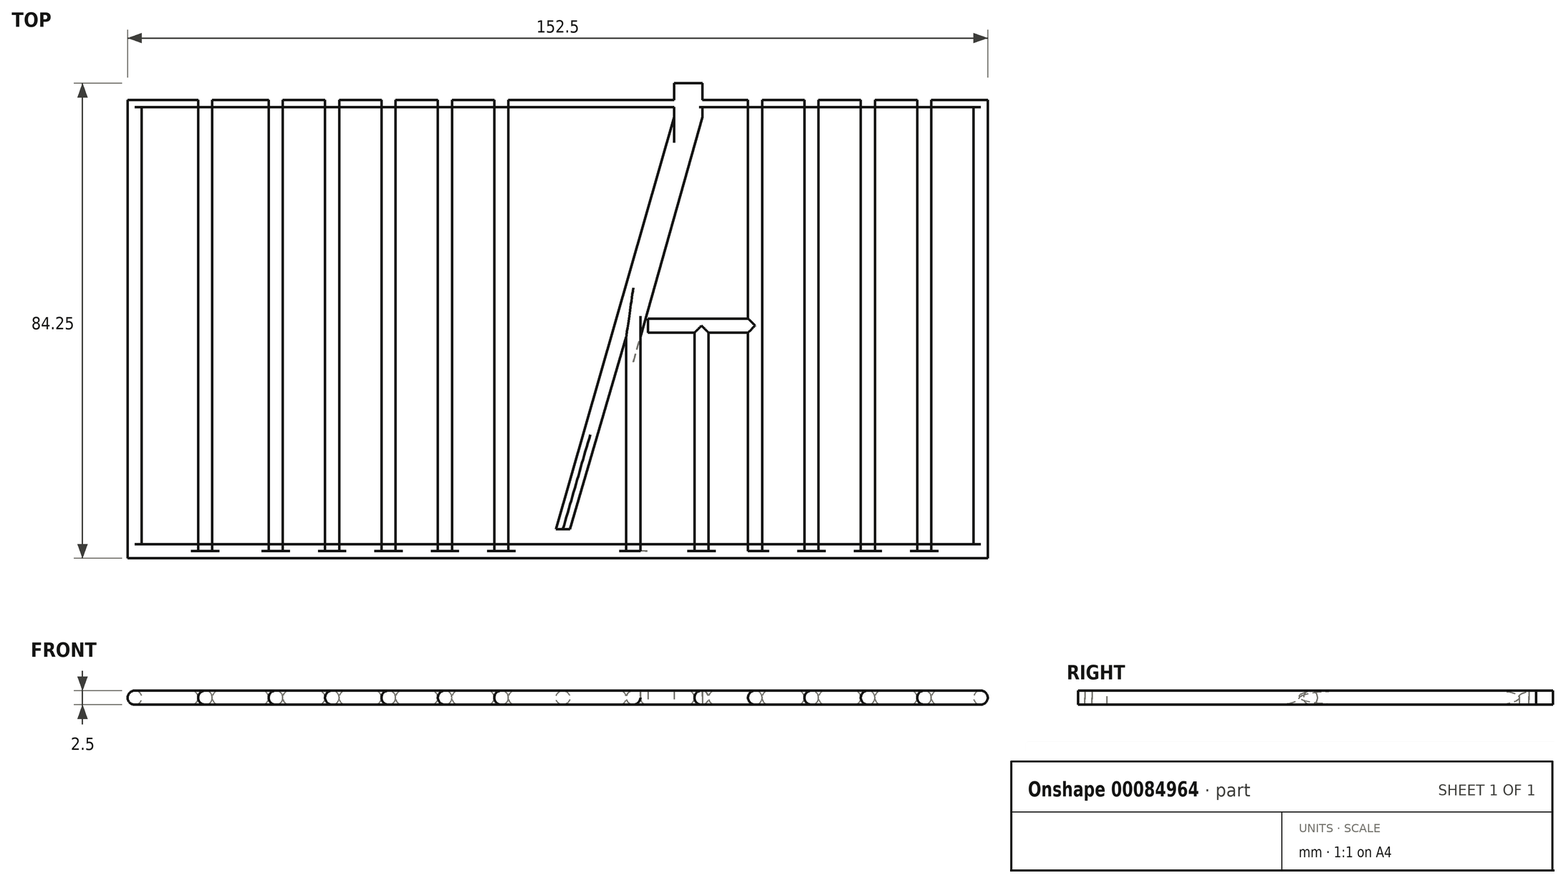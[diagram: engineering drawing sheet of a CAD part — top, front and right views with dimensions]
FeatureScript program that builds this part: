
annotation { "Feature Type Name" : "Feature", "Feature Type Description" : "" }
export const myFeature = defineFeature(function(context is Context, id is Id, definition is map)
    precondition{}
    {
        {
            var Q0;
            Q0=qCreatedBy(makeId("Top.planeOp"),FACE);
            var sketch = newSketch(context, id + "F0", { "sketchPlane" : qUnion([Q0])});
            skLineSegment(sketch, "E0", {"start": v(0, 0) * mm, "end": v(75, 0) * mm});
            skLineSegment(sketch, "E1", {"start": v(0, 0) * mm, "end": v(-75, 0) * mm});
            skLineSegment(sketch, "E2", {"start": v(-75, 0) * mm, "end": v(-75, 80) * mm});
            skLineSegment(sketch, "E3", {"start": v(-75, 80) * mm, "end": v(75, 80) * mm});
            skLineSegment(sketch, "E4", {"start": v(75, 80) * mm, "end": v(75, 0) * mm});
            skLineSegment(sketch, "E5.bottom", {"start": v(-73.75, 0) * mm, "end": v(-76.25, 0) * mm});
            skLineSegment(sketch, "E5.top", {"start": v(-73.75, 80) * mm, "end": v(-76.25, 80) * mm});
            skLineSegment(sketch, "E5.left", {"start": v(-73.75, 0) * mm, "end": v(-73.75, 80) * mm});
            skLineSegment(sketch, "E5.right", {"start": v(-76.25, 0) * mm, "end": v(-76.25, 80) * mm});
            skPoint(sketch, "E5.middle", {"position": v(-75, 40) * mm});
            skLineSegment(sketch, "E6.bottom", {"start": v(76.25, 0) * mm, "end": v(73.75, 0) * mm});
            skLineSegment(sketch, "E6.top", {"start": v(76.25, 80) * mm, "end": v(73.75, 80) * mm});
            skLineSegment(sketch, "E6.left", {"start": v(76.25, 0) * mm, "end": v(76.25, 80) * mm});
            skLineSegment(sketch, "E6.right", {"start": v(73.75, 0) * mm, "end": v(73.75, 80) * mm});
            skPoint(sketch, "E6.middle", {"position": v(75, 40) * mm});
            skLineSegment(sketch, "E7.bottom", {"start": v(-76.25, 81.25) * mm, "end": v(76.25, 81.25) * mm});
            skLineSegment(sketch, "E7.top", {"start": v(-76.25, 78.75) * mm, "end": v(76.25, 78.75) * mm});
            skLineSegment(sketch, "E7.left", {"start": v(-76.25, 81.25) * mm, "end": v(-76.25, 78.75) * mm});
            skLineSegment(sketch, "E7.right", {"start": v(76.25, 81.25) * mm, "end": v(76.25, 78.75) * mm});
            skPoint(sketch, "E7.middle", {"position": v(0, 80) * mm});
            skLineSegment(sketch, "E8.bottom", {"start": v(-76.25, -1.25) * mm, "end": v(76.25, -1.25) * mm});
            skLineSegment(sketch, "E8.top", {"start": v(-76.25, 1.25) * mm, "end": v(76.25, 1.25) * mm});
            skLineSegment(sketch, "E8.left", {"start": v(-76.25, -1.25) * mm, "end": v(-76.25, 1.25) * mm});
            skLineSegment(sketch, "E8.right", {"start": v(76.25, -1.25) * mm, "end": v(76.25, 1.25) * mm});
            skPoint(sketch, "E8.middle", {"position": v(0, 0) * mm});
            skLineSegment(sketch, "E9.bottom", {"start": v(-61.25, 0) * mm, "end": v(-63.75, 0) * mm});
            skLineSegment(sketch, "E9.top", {"start": v(-61.25, 80) * mm, "end": v(-63.75, 80) * mm});
            skLineSegment(sketch, "E9.left", {"start": v(-61.25, 0) * mm, "end": v(-61.25, 80) * mm});
            skLineSegment(sketch, "E9.right", {"start": v(-63.75, 0) * mm, "end": v(-63.75, 80) * mm});
            skPoint(sketch, "E9.middle", {"position": v(-62.5, 40) * mm});
            skLineSegment(sketch, "E10.bottom", {"start": v(-48.75, 0) * mm, "end": v(-51.25, 0) * mm});
            skLineSegment(sketch, "E10.top", {"start": v(-48.75, 80) * mm, "end": v(-51.25, 80) * mm});
            skLineSegment(sketch, "E10.left", {"start": v(-48.75, 0) * mm, "end": v(-48.75, 80) * mm});
            skLineSegment(sketch, "E10.right", {"start": v(-51.25, 0) * mm, "end": v(-51.25, 80) * mm});
            skPoint(sketch, "E10.middle", {"position": v(-50, 40) * mm});
            skLineSegment(sketch, "E11.bottom", {"start": v(14.66, 0) * mm, "end": v(12.16, 0) * mm});
            skLineSegment(sketch, "E11.top", {"start": v(14.66, 38) * mm, "end": v(12.16, 38) * mm});
            skLineSegment(sketch, "E11.left", {"start": v(14.66, 0) * mm, "end": v(14.66, 38) * mm});
            skLineSegment(sketch, "E11.right", {"start": v(12.16, 0) * mm, "end": v(12.16, 38) * mm});
            skPoint(sketch, "E11.middle", {"position": v(13.4, 19) * mm});
            skLineSegment(sketch, "E12.bottom", {"start": v(25.63, 77) * mm, "end": v(20.63, 77) * mm});
            skLineSegment(sketch, "E12.top", {"start": v(25.63, 83) * mm, "end": v(20.63, 83) * mm});
            skLineSegment(sketch, "E12.left", {"start": v(25.63, 77) * mm, "end": v(25.63, 83) * mm});
            skLineSegment(sketch, "E12.right", {"start": v(20.63, 77) * mm, "end": v(20.63, 83) * mm});
            skPoint(sketch, "E12.middle", {"position": v(23.13, 80) * mm});
            skLineSegment(sketch, "E13", {"start": v(25.63, 77) * mm, "end": v(14.66, 38) * mm});
            skLineSegment(sketch, "E14", {"start": v(12.16, 38) * mm, "end": v(23.13, 77) * mm});
            skLineSegment(sketch, "E15", {"start": v(12.16, 38) * mm, "end": v(2.16, 3.89) * mm});
            skLineSegment(sketch, "E16", {"start": v(20.63, 77) * mm, "end": v(-0.34, 3.89) * mm});
            skLineSegment(sketch, "E17", {"start": v(-0.34, 3.89) * mm, "end": v(2.16, 3.89) * mm});
            skLineSegment(sketch, "E18.bottom", {"start": v(-38.75, 0) * mm, "end": v(-41.25, 0) * mm});
            skLineSegment(sketch, "E18.top", {"start": v(-38.75, 80) * mm, "end": v(-41.25, 80) * mm});
            skLineSegment(sketch, "E18.left", {"start": v(-38.75, 0) * mm, "end": v(-38.75, 80) * mm});
            skLineSegment(sketch, "E18.right", {"start": v(-41.25, 0) * mm, "end": v(-41.25, 80) * mm});
            skPoint(sketch, "E18.middle", {"position": v(-40, 40) * mm});
            skLineSegment(sketch, "E19.bottom", {"start": v(-28.75, 0) * mm, "end": v(-31.25, 0) * mm});
            skLineSegment(sketch, "E19.top", {"start": v(-28.75, 80) * mm, "end": v(-31.25, 80) * mm});
            skLineSegment(sketch, "E19.left", {"start": v(-28.75, 0) * mm, "end": v(-28.75, 80) * mm});
            skLineSegment(sketch, "E19.right", {"start": v(-31.25, 0) * mm, "end": v(-31.25, 80) * mm});
            skPoint(sketch, "E19.middle", {"position": v(-30, 40) * mm});
            skLineSegment(sketch, "E20.bottom", {"start": v(-18.75, 0) * mm, "end": v(-21.25, 0) * mm});
            skLineSegment(sketch, "E20.top", {"start": v(-18.75, 80) * mm, "end": v(-21.25, 80) * mm});
            skLineSegment(sketch, "E20.left", {"start": v(-18.75, 0) * mm, "end": v(-18.75, 80) * mm});
            skLineSegment(sketch, "E20.right", {"start": v(-21.25, 0) * mm, "end": v(-21.25, 80) * mm});
            skPoint(sketch, "E20.middle", {"position": v(-20, 40) * mm});
            skLineSegment(sketch, "E21.bottom", {"start": v(-8.75, 0) * mm, "end": v(-11.25, 0) * mm});
            skLineSegment(sketch, "E21.top", {"start": v(-8.75, 80) * mm, "end": v(-11.25, 80) * mm});
            skLineSegment(sketch, "E21.left", {"start": v(-8.75, 0) * mm, "end": v(-8.75, 80) * mm});
            skLineSegment(sketch, "E21.right", {"start": v(-11.25, 0) * mm, "end": v(-11.25, 80) * mm});
            skPoint(sketch, "E21.middle", {"position": v(-10, 40) * mm});
            skLineSegment(sketch, "E22.bottom", {"start": v(66.25, 0) * mm, "end": v(63.75, 0) * mm});
            skLineSegment(sketch, "E22.top", {"start": v(66.25, 80) * mm, "end": v(63.75, 80) * mm});
            skLineSegment(sketch, "E22.left", {"start": v(66.25, 0) * mm, "end": v(66.25, 80) * mm});
            skLineSegment(sketch, "E22.right", {"start": v(63.75, 0) * mm, "end": v(63.75, 80) * mm});
            skPoint(sketch, "E22.middle", {"position": v(65, 40) * mm});
            skLineSegment(sketch, "E23.bottom", {"start": v(56.25, 0) * mm, "end": v(53.75, 0) * mm});
            skLineSegment(sketch, "E23.top", {"start": v(56.25, 80) * mm, "end": v(53.75, 80) * mm});
            skLineSegment(sketch, "E23.left", {"start": v(56.25, 0) * mm, "end": v(56.25, 80) * mm});
            skLineSegment(sketch, "E23.right", {"start": v(53.75, 0) * mm, "end": v(53.75, 80) * mm});
            skPoint(sketch, "E23.middle", {"position": v(55, 40) * mm});
            skLineSegment(sketch, "E24.bottom", {"start": v(46.25, 0) * mm, "end": v(43.75, 0) * mm});
            skLineSegment(sketch, "E24.top", {"start": v(46.25, 80) * mm, "end": v(43.75, 80) * mm});
            skLineSegment(sketch, "E24.left", {"start": v(46.25, 0) * mm, "end": v(46.25, 80) * mm});
            skLineSegment(sketch, "E24.right", {"start": v(43.75, 0) * mm, "end": v(43.75, 80) * mm});
            skPoint(sketch, "E24.middle", {"position": v(45, 40) * mm});
            skLineSegment(sketch, "E25.bottom", {"start": v(36.25, 0) * mm, "end": v(33.75, 0) * mm});
            skLineSegment(sketch, "E25.top", {"start": v(36.25, 80) * mm, "end": v(33.75, 80) * mm});
            skLineSegment(sketch, "E25.left", {"start": v(36.25, 0) * mm, "end": v(36.25, 80) * mm});
            skLineSegment(sketch, "E25.right", {"start": v(33.75, 0) * mm, "end": v(33.75, 80) * mm});
            skPoint(sketch, "E25.middle", {"position": v(35, 40) * mm});
            skPoint(sketch, "E25.middle.positionSnap0", {"position": v(43.75, 40) * mm});
            skPoint(sketch, "E25.centerSnap0", {"position": v(43.75, 40) * mm});
            skLineSegment(sketch, "E26.bottom", {"start": v(35, 38.75) * mm, "end": v(16, 38.75) * mm});
            skLineSegment(sketch, "E26.top", {"start": v(35, 41.25) * mm, "end": v(16, 41.25) * mm});
            skLineSegment(sketch, "E26.left", {"start": v(35, 38.75) * mm, "end": v(35, 41.25) * mm});
            skLineSegment(sketch, "E26.right", {"start": v(16, 38.75) * mm, "end": v(16, 41.25) * mm});
            skPoint(sketch, "E26.middle", {"position": v(25.5, 40) * mm});
            skLineSegment(sketch, "E27.bottom", {"start": v(26.75, 0) * mm, "end": v(24.25, 0) * mm});
            skLineSegment(sketch, "E27.top", {"start": v(26.75, 40) * mm, "end": v(24.25, 40) * mm});
            skLineSegment(sketch, "E27.left", {"start": v(26.75, 0) * mm, "end": v(26.75, 40) * mm});
            skLineSegment(sketch, "E27.right", {"start": v(24.25, 0) * mm, "end": v(24.25, 40) * mm});
            skPoint(sketch, "E27.middle", {"position": v(25.5, 20) * mm});
            skSolve(sketch);
        }
        {
            var Q0;
            {var subQ0=sQuery(id+"F0.wireOp",EDGE,"E8.bottom");Q0=makeQuery(id+"F0.imprint","IMPRINT",FACE,{"disambiguationData":[TD([[makeQuery(id+"F0.imprint","IMPRINT",EDGE,{"derivedFrom":subQ0}),1.0]])]});}
            var Q1;
            {var subQ3=sQuery(id+"F0.wireOp",EDGE,"E8.top");var subQ7=sQuery(id+"F0.wireOp",EDGE,"E21.left");var subQ9=makeQuery(id+"F0.imprint","INTERSECT",VERTEX,{"derivedFrom":[subQ3,subQ7]});Q1=makeQuery(id+"F0.imprint","IMPRINT",FACE,{"disambiguationData":[TD([[makeQuery(id+"F0.imprint","IMPRINT",EDGE,{"disambiguationData":[TD([[subQ9,-1.0]])],"derivedFrom":subQ3}),-1.0]])]});}
            var Q2;
            {var subQ5=sQuery(id+"F0.wireOp",EDGE,"E11.bottom");Q2=makeQuery(id+"F0.imprint","IMPRINT",FACE,{"disambiguationData":[TD([[makeQuery(id+"F0.imprint","IMPRINT",EDGE,{"derivedFrom":subQ5}),-1.0]])]});}
            var Q3;
            {var subQ0=sQuery(id+"F0.wireOp",EDGE,"E11.left");var subQ5=sQuery(id+"F0.wireOp",EDGE,"E8.top");var subQ6=makeQuery(id+"F0.imprint","INTERSECT",VERTEX,{"derivedFrom":[subQ5,subQ0]});Q3=makeQuery(id+"F0.imprint","IMPRINT",FACE,{"disambiguationData":[TD([[makeQuery(id+"F0.imprint","IMPRINT",EDGE,{"disambiguationData":[TD([[subQ6,-1.0]])],"derivedFrom":subQ5}),-1.0]])]});}
            var Q4;
            {var subQ5=sQuery(id+"F0.wireOp",EDGE,"E11.top");Q4=makeQuery(id+"F0.imprint","IMPRINT",FACE,{"disambiguationData":[TD([[makeQuery(id+"F0.imprint","IMPRINT",EDGE,{"derivedFrom":subQ5}),1.0]])]});}
            var Q5;
            {var subQ1=sQuery(id+"F0.wireOp",EDGE,"E14");Q5=makeQuery(id+"F0.imprint","IMPRINT",FACE,{"disambiguationData":[TD([[makeQuery(id+"F0.imprint","IMPRINT",EDGE,{"derivedFrom":subQ1}),1.0]])]});}
            var Q6;
            Q6=makeQuery(id+"F0.imprint","IMPRINT",FACE,{"disambiguationData":[TD([[makeQuery(id+"F0.imprint","IMPRINT",EDGE,{"derivedFrom":sQuery(id+"F0.wireOp",EDGE,"E11.top")}),-1.0]])]});
            var Q7;
            {var subQ3=sQuery(id+"F0.wireOp",EDGE,"E7.top");var subQ5=sQuery(id+"F0.wireOp",EDGE,"E12.right");var subQ8=makeQuery(id+"F0.imprint","INTERSECT",VERTEX,{"derivedFrom":[subQ3,subQ5]});Q7=makeQuery(id+"F0.imprint","IMPRINT",FACE,{"disambiguationData":[TD([[makeQuery(id+"F0.imprint","IMPRINT",EDGE,{"disambiguationData":[TD([[subQ8,-1.0]])],"derivedFrom":subQ3}),-1.0]])]});}
            var Q8;
            {var subQ0=sQuery(id+"F0.wireOp",EDGE,"E12.right");var subQ1=sQuery(id+"F0.wireOp",EDGE,"E3");var subQ2=makeQuery(id+"F0.imprint","INTERSECT",VERTEX,{"derivedFrom":[subQ1,subQ0]});Q8=makeQuery(id+"F0.imprint","IMPRINT",FACE,{"disambiguationData":[TD([[makeQuery(id+"F0.imprint","IMPRINT",EDGE,{"disambiguationData":[TD([[subQ2,-1.0]])],"derivedFrom":subQ1}),-1.0]])]});}
            var Q9;
            {var subQ5=sQuery(id+"F0.wireOp",EDGE,"E12.top");Q9=makeQuery(id+"F0.imprint","IMPRINT",FACE,{"disambiguationData":[TD([[makeQuery(id+"F0.imprint","IMPRINT",EDGE,{"derivedFrom":subQ5}),1.0]])]});}
            var Q10;
            {var subQ0=sQuery(id+"F0.wireOp",EDGE,"E12.right");var subQ1=sQuery(id+"F0.wireOp",EDGE,"E3");var subQ2=makeQuery(id+"F0.imprint","INTERSECT",VERTEX,{"derivedFrom":[subQ1,subQ0]});Q10=makeQuery(id+"F0.imprint","IMPRINT",FACE,{"disambiguationData":[TD([[makeQuery(id+"F0.imprint","IMPRINT",EDGE,{"disambiguationData":[TD([[subQ2,-1.0]])],"derivedFrom":subQ1}),1.0]])]});}
            var Q11;
            {var subQ0=sQuery(id+"F0.wireOp",EDGE,"E21.left");var subQ5=sQuery(id+"F0.wireOp",EDGE,"E7.top");var subQ6=makeQuery(id+"F0.imprint","INTERSECT",VERTEX,{"derivedFrom":[subQ5,subQ0]});Q11=makeQuery(id+"F0.imprint","IMPRINT",FACE,{"disambiguationData":[TD([[makeQuery(id+"F0.imprint","IMPRINT",EDGE,{"disambiguationData":[TD([[subQ6,-1.0]])],"derivedFrom":subQ5}),1.0]])]});}
            var Q12;
            {var subQ15=sQuery(id+"F0.wireOp",EDGE,"E9.top");Q12=makeQuery(id+"F0.imprint","IMPRINT",FACE,{"disambiguationData":[TD([[makeQuery(id+"F0.imprint","IMPRINT",EDGE,{"derivedFrom":subQ15}),-1.0]])]});}
            var Q13;
            {var subQ0=sQuery(id+"F0.wireOp",EDGE,"E27.right");var subQ1=sQuery(id+"F0.wireOp",EDGE,"E8.top");var subQ2=makeQuery(id+"F0.imprint","INTERSECT",VERTEX,{"derivedFrom":[subQ1,subQ0]});Q13=makeQuery(id+"F0.imprint","IMPRINT",FACE,{"disambiguationData":[TD([[makeQuery(id+"F0.imprint","IMPRINT",EDGE,{"disambiguationData":[TD([[subQ2,-1.0]])],"derivedFrom":subQ1}),1.0]])]});}
            var Q14;
            {var subQ0=sQuery(id+"F0.wireOp",EDGE,"E26.right");Q14=makeQuery(id+"F0.imprint","IMPRINT",FACE,{"disambiguationData":[TD([[makeQuery(id+"F0.imprint","IMPRINT",EDGE,{"derivedFrom":subQ0}),-1.0]])]});}
            var Q15;
            {var subQ9=sQuery(id+"F0.wireOp",EDGE,"E26.left");Q15=makeQuery(id+"F0.imprint","IMPRINT",FACE,{"disambiguationData":[TD([[makeQuery(id+"F0.imprint","IMPRINT",EDGE,{"derivedFrom":subQ9}),-1.0]])]});}
            var Q16;
            {var subQ0=sQuery(id+"F0.wireOp",EDGE,"E23.right");var subQ1=sQuery(id+"F0.wireOp",EDGE,"E7.top");var subQ2=makeQuery(id+"F0.imprint","INTERSECT",VERTEX,{"derivedFrom":[subQ1,subQ0]});Q16=makeQuery(id+"F0.imprint","IMPRINT",FACE,{"disambiguationData":[TD([[makeQuery(id+"F0.imprint","IMPRINT",EDGE,{"disambiguationData":[TD([[subQ2,-1.0]])],"derivedFrom":subQ1}),-1.0]])]});}
            var Q17;
            {var subQ0=sQuery(id+"F0.wireOp",EDGE,"E22.right");var subQ1=sQuery(id+"F0.wireOp",EDGE,"E7.top");var subQ2=makeQuery(id+"F0.imprint","INTERSECT",VERTEX,{"derivedFrom":[subQ1,subQ0]});Q17=makeQuery(id+"F0.imprint","IMPRINT",FACE,{"disambiguationData":[TD([[makeQuery(id+"F0.imprint","IMPRINT",EDGE,{"disambiguationData":[TD([[subQ2,-1.0]])],"derivedFrom":subQ1}),-1.0]])]});}
            var Q18;
            {var subQ5=sQuery(id+"F0.wireOp",EDGE,"E27.bottom");Q18=makeQuery(id+"F0.imprint","IMPRINT",FACE,{"disambiguationData":[TD([[makeQuery(id+"F0.imprint","IMPRINT",EDGE,{"derivedFrom":subQ5}),-1.0]])]});}
            var Q19;
            {var subQ3=sQuery(id+"F0.wireOp",EDGE,"E27.left");var subQ5=sQuery(id+"F0.wireOp",EDGE,"E8.top");var subQ6=makeQuery(id+"F0.imprint","INTERSECT",VERTEX,{"derivedFrom":[subQ5,subQ3]});Q19=makeQuery(id+"F0.imprint","IMPRINT",FACE,{"disambiguationData":[TD([[makeQuery(id+"F0.imprint","IMPRINT",EDGE,{"disambiguationData":[TD([[subQ6,-1.0]])],"derivedFrom":subQ5}),-1.0]])]});}
            var Q20;
            {var subQ5=sQuery(id+"F0.wireOp",EDGE,"E25.bottom");Q20=makeQuery(id+"F0.imprint","IMPRINT",FACE,{"disambiguationData":[TD([[makeQuery(id+"F0.imprint","IMPRINT",EDGE,{"derivedFrom":subQ5}),-1.0]])]});}
            var Q21;
            {var subQ3=sQuery(id+"F0.wireOp",EDGE,"E25.left");var subQ5=sQuery(id+"F0.wireOp",EDGE,"E8.top");var subQ6=makeQuery(id+"F0.imprint","INTERSECT",VERTEX,{"derivedFrom":[subQ5,subQ3]});Q21=makeQuery(id+"F0.imprint","IMPRINT",FACE,{"disambiguationData":[TD([[makeQuery(id+"F0.imprint","IMPRINT",EDGE,{"disambiguationData":[TD([[subQ6,-1.0]])],"derivedFrom":subQ5}),-1.0]])]});}
            var Q22;
            {var subQ5=sQuery(id+"F0.wireOp",EDGE,"E24.bottom");Q22=makeQuery(id+"F0.imprint","IMPRINT",FACE,{"disambiguationData":[TD([[makeQuery(id+"F0.imprint","IMPRINT",EDGE,{"derivedFrom":subQ5}),-1.0]])]});}
            var Q23;
            {var subQ0=sQuery(id+"F0.wireOp",EDGE,"E24.right");var subQ1=sQuery(id+"F0.wireOp",EDGE,"E7.top");var subQ2=makeQuery(id+"F0.imprint","INTERSECT",VERTEX,{"derivedFrom":[subQ1,subQ0]});Q23=makeQuery(id+"F0.imprint","IMPRINT",FACE,{"disambiguationData":[TD([[makeQuery(id+"F0.imprint","IMPRINT",EDGE,{"disambiguationData":[TD([[subQ2,-1.0]])],"derivedFrom":subQ1}),-1.0]])]});}
            var Q24;
            {var subQ3=sQuery(id+"F0.wireOp",EDGE,"E23.left");var subQ5=sQuery(id+"F0.wireOp",EDGE,"E8.top");var subQ7=makeQuery(id+"F0.imprint","INTERSECT",VERTEX,{"derivedFrom":[subQ5,subQ3]});Q24=makeQuery(id+"F0.imprint","IMPRINT",FACE,{"disambiguationData":[TD([[makeQuery(id+"F0.imprint","IMPRINT",EDGE,{"disambiguationData":[TD([[subQ7,-1.0]])],"derivedFrom":subQ5}),-1.0]])]});}
            var Q25;
            {var subQ5=sQuery(id+"F0.wireOp",EDGE,"E23.bottom");Q25=makeQuery(id+"F0.imprint","IMPRINT",FACE,{"disambiguationData":[TD([[makeQuery(id+"F0.imprint","IMPRINT",EDGE,{"derivedFrom":subQ5}),-1.0]])]});}
            var Q26;
            {var subQ3=sQuery(id+"F0.wireOp",EDGE,"E24.left");var subQ5=sQuery(id+"F0.wireOp",EDGE,"E8.top");var subQ6=makeQuery(id+"F0.imprint","INTERSECT",VERTEX,{"derivedFrom":[subQ5,subQ3]});Q26=makeQuery(id+"F0.imprint","IMPRINT",FACE,{"disambiguationData":[TD([[makeQuery(id+"F0.imprint","IMPRINT",EDGE,{"disambiguationData":[TD([[subQ6,-1.0]])],"derivedFrom":subQ5}),-1.0]])]});}
            var Q27;
            {var subQ5=sQuery(id+"F0.wireOp",EDGE,"E22.bottom");Q27=makeQuery(id+"F0.imprint","IMPRINT",FACE,{"disambiguationData":[TD([[makeQuery(id+"F0.imprint","IMPRINT",EDGE,{"derivedFrom":subQ5}),-1.0]])]});}
            var Q28;
            {var subQ0=sQuery(id+"F0.wireOp",EDGE,"E6.bottom");var subQ1=sQuery(id+"F0.wireOp",EDGE,"E4");var subQ2=makeQuery(id+"F0.imprint","INTERSECT",VERTEX,{"derivedFrom":[subQ1,subQ0]});Q28=makeQuery(id+"F0.imprint","IMPRINT",FACE,{"disambiguationData":[TD([[makeQuery(id+"F0.imprint","IMPRINT",EDGE,{"disambiguationData":[TD([[subQ2,1.0]])],"derivedFrom":subQ1}),-1.0]])]});}
            var Q29;
            {var subQ0=sQuery(id+"F0.wireOp",EDGE,"E6.right");var subQ5=sQuery(id+"F0.wireOp",EDGE,"E8.top");var subQ6=makeQuery(id+"F0.imprint","INTERSECT",VERTEX,{"derivedFrom":[subQ0,subQ5]});Q29=makeQuery(id+"F0.imprint","IMPRINT",FACE,{"disambiguationData":[TD([[makeQuery(id+"F0.imprint","IMPRINT",EDGE,{"disambiguationData":[TD([[subQ6,1.0]])],"derivedFrom":subQ5}),-1.0]])]});}
            var Q30;
            {var subQ0=sQuery(id+"F0.wireOp",EDGE,"E6.bottom");var subQ1=sQuery(id+"F0.wireOp",EDGE,"E4");var subQ2=makeQuery(id+"F0.imprint","INTERSECT",VERTEX,{"derivedFrom":[subQ1,subQ0]});Q30=makeQuery(id+"F0.imprint","IMPRINT",FACE,{"disambiguationData":[TD([[makeQuery(id+"F0.imprint","IMPRINT",EDGE,{"disambiguationData":[TD([[subQ2,1.0]])],"derivedFrom":subQ1}),1.0]])]});}
            var Q31;
            {var subQ5=sQuery(id+"F0.wireOp",EDGE,"E6.left");Q31=makeQuery(id+"F0.imprint","IMPRINT",FACE,{"disambiguationData":[TD([[makeQuery(id+"F0.imprint","IMPRINT",EDGE,{"derivedFrom":subQ5}),1.0]])]});}
            var Q32;
            {var subQ0=sQuery(id+"F0.wireOp",EDGE,"E7.top");var subQ1=sQuery(id+"F0.wireOp",EDGE,"E4");var subQ2=makeQuery(id+"F0.imprint","INTERSECT",VERTEX,{"derivedFrom":[subQ1,subQ0]});Q32=makeQuery(id+"F0.imprint","IMPRINT",FACE,{"disambiguationData":[TD([[makeQuery(id+"F0.imprint","IMPRINT",EDGE,{"disambiguationData":[TD([[subQ2,-1.0]])],"derivedFrom":subQ1}),-1.0]])]});}
            var Q33;
            {var subQ0=sQuery(id+"F0.wireOp",EDGE,"E6.top");var subQ1=sQuery(id+"F0.wireOp",EDGE,"E4");var subQ2=makeQuery(id+"F0.imprint","INTERSECT",VERTEX,{"derivedFrom":[subQ1,subQ0]});Q33=makeQuery(id+"F0.imprint","IMPRINT",FACE,{"disambiguationData":[TD([[makeQuery(id+"F0.imprint","IMPRINT",EDGE,{"disambiguationData":[TD([[subQ2,-1.0]])],"derivedFrom":subQ1}),-1.0]])]});}
            var Q34;
            {var subQ0=sQuery(id+"F0.wireOp",EDGE,"E6.top");var subQ1=sQuery(id+"F0.wireOp",EDGE,"E4");var subQ2=makeQuery(id+"F0.imprint","INTERSECT",VERTEX,{"derivedFrom":[subQ1,subQ0]});Q34=makeQuery(id+"F0.imprint","IMPRINT",FACE,{"disambiguationData":[TD([[makeQuery(id+"F0.imprint","IMPRINT",EDGE,{"disambiguationData":[TD([[subQ2,-1.0]])],"derivedFrom":subQ1}),1.0]])]});}
            var Q35;
            {var subQ5=sQuery(id+"F0.wireOp",EDGE,"E24.top");Q35=makeQuery(id+"F0.imprint","IMPRINT",FACE,{"disambiguationData":[TD([[makeQuery(id+"F0.imprint","IMPRINT",EDGE,{"derivedFrom":subQ5}),1.0]])]});}
            var Q36;
            {var subQ3=sQuery(id+"F0.wireOp",EDGE,"E23.left");var subQ5=sQuery(id+"F0.wireOp",EDGE,"E7.top");var subQ6=makeQuery(id+"F0.imprint","INTERSECT",VERTEX,{"derivedFrom":[subQ5,subQ3]});Q36=makeQuery(id+"F0.imprint","IMPRINT",FACE,{"disambiguationData":[TD([[makeQuery(id+"F0.imprint","IMPRINT",EDGE,{"disambiguationData":[TD([[subQ6,-1.0]])],"derivedFrom":subQ5}),1.0]])]});}
            var Q37;
            {var subQ5=sQuery(id+"F0.wireOp",EDGE,"E23.top");Q37=makeQuery(id+"F0.imprint","IMPRINT",FACE,{"disambiguationData":[TD([[makeQuery(id+"F0.imprint","IMPRINT",EDGE,{"derivedFrom":subQ5}),1.0]])]});}
            var Q38;
            {var subQ11=sQuery(id+"F0.wireOp",EDGE,"E22.top");Q38=makeQuery(id+"F0.imprint","IMPRINT",FACE,{"disambiguationData":[TD([[makeQuery(id+"F0.imprint","IMPRINT",EDGE,{"derivedFrom":subQ11}),-1.0]])]});}
            var Q39;
            {var subQ3=sQuery(id+"F0.wireOp",EDGE,"E24.left");var subQ5=sQuery(id+"F0.wireOp",EDGE,"E7.top");var subQ6=makeQuery(id+"F0.imprint","INTERSECT",VERTEX,{"derivedFrom":[subQ5,subQ3]});Q39=makeQuery(id+"F0.imprint","IMPRINT",FACE,{"disambiguationData":[TD([[makeQuery(id+"F0.imprint","IMPRINT",EDGE,{"disambiguationData":[TD([[subQ6,-1.0]])],"derivedFrom":subQ5}),1.0]])]});}
            var Q40;
            {var subQ0=sQuery(id+"F0.wireOp",EDGE,"E6.right");var subQ5=sQuery(id+"F0.wireOp",EDGE,"E7.top");var subQ6=makeQuery(id+"F0.imprint","INTERSECT",VERTEX,{"derivedFrom":[subQ0,subQ5]});Q40=makeQuery(id+"F0.imprint","IMPRINT",FACE,{"disambiguationData":[TD([[makeQuery(id+"F0.imprint","IMPRINT",EDGE,{"disambiguationData":[TD([[subQ6,1.0]])],"derivedFrom":subQ5}),1.0]])]});}
            var Q41;
            {var subQ5=sQuery(id+"F0.wireOp",EDGE,"E22.top");Q41=makeQuery(id+"F0.imprint","IMPRINT",FACE,{"disambiguationData":[TD([[makeQuery(id+"F0.imprint","IMPRINT",EDGE,{"derivedFrom":subQ5}),1.0]])]});}
            var Q42;
            {var subQ3=sQuery(id+"F0.wireOp",EDGE,"E12.left");var subQ5=sQuery(id+"F0.wireOp",EDGE,"E7.top");var subQ6=makeQuery(id+"F0.imprint","INTERSECT",VERTEX,{"derivedFrom":[subQ5,subQ3]});Q42=makeQuery(id+"F0.imprint","IMPRINT",FACE,{"disambiguationData":[TD([[makeQuery(id+"F0.imprint","IMPRINT",EDGE,{"disambiguationData":[TD([[subQ6,-1.0]])],"derivedFrom":subQ5}),1.0]])]});}
            var Q43;
            {var subQ5=sQuery(id+"F0.wireOp",EDGE,"E25.top");Q43=makeQuery(id+"F0.imprint","IMPRINT",FACE,{"disambiguationData":[TD([[makeQuery(id+"F0.imprint","IMPRINT",EDGE,{"derivedFrom":subQ5}),1.0]])]});}
            var Q44;
            {var subQ3=sQuery(id+"F0.wireOp",EDGE,"E25.left");var subQ5=sQuery(id+"F0.wireOp",EDGE,"E7.top");var subQ6=makeQuery(id+"F0.imprint","INTERSECT",VERTEX,{"derivedFrom":[subQ5,subQ3]});Q44=makeQuery(id+"F0.imprint","IMPRINT",FACE,{"disambiguationData":[TD([[makeQuery(id+"F0.imprint","IMPRINT",EDGE,{"disambiguationData":[TD([[subQ6,-1.0]])],"derivedFrom":subQ5}),1.0]])]});}
            var Q45;
            {var subQ0=sQuery(id+"F0.wireOp",EDGE,"E10.left");var subQ5=sQuery(id+"F0.wireOp",EDGE,"E7.top");var subQ7=makeQuery(id+"F0.imprint","INTERSECT",VERTEX,{"derivedFrom":[subQ5,subQ0]});Q45=makeQuery(id+"F0.imprint","IMPRINT",FACE,{"disambiguationData":[TD([[makeQuery(id+"F0.imprint","IMPRINT",EDGE,{"disambiguationData":[TD([[subQ7,-1.0]])],"derivedFrom":subQ5}),1.0]])]});}
            var Q46;
            {var subQ0=sQuery(id+"F0.wireOp",EDGE,"E19.left");var subQ5=sQuery(id+"F0.wireOp",EDGE,"E7.top");var subQ7=makeQuery(id+"F0.imprint","INTERSECT",VERTEX,{"derivedFrom":[subQ5,subQ0]});Q46=makeQuery(id+"F0.imprint","IMPRINT",FACE,{"disambiguationData":[TD([[makeQuery(id+"F0.imprint","IMPRINT",EDGE,{"disambiguationData":[TD([[subQ7,-1.0]])],"derivedFrom":subQ5}),1.0]])]});}
            var Q47;
            {var subQ0=sQuery(id+"F0.wireOp",EDGE,"E9.left");var subQ5=sQuery(id+"F0.wireOp",EDGE,"E7.top");var subQ6=makeQuery(id+"F0.imprint","INTERSECT",VERTEX,{"derivedFrom":[subQ5,subQ0]});Q47=makeQuery(id+"F0.imprint","IMPRINT",FACE,{"disambiguationData":[TD([[makeQuery(id+"F0.imprint","IMPRINT",EDGE,{"disambiguationData":[TD([[subQ6,-1.0]])],"derivedFrom":subQ5}),1.0]])]});}
            var Q48;
            {var subQ0=sQuery(id+"F0.wireOp",EDGE,"E18.left");var subQ5=sQuery(id+"F0.wireOp",EDGE,"E7.top");var subQ6=makeQuery(id+"F0.imprint","INTERSECT",VERTEX,{"derivedFrom":[subQ5,subQ0]});Q48=makeQuery(id+"F0.imprint","IMPRINT",FACE,{"disambiguationData":[TD([[makeQuery(id+"F0.imprint","IMPRINT",EDGE,{"disambiguationData":[TD([[subQ6,-1.0]])],"derivedFrom":subQ5}),1.0]])]});}
            var Q49;
            {var subQ0=sQuery(id+"F0.wireOp",EDGE,"E5.left");var subQ5=sQuery(id+"F0.wireOp",EDGE,"E7.top");var subQ6=makeQuery(id+"F0.imprint","INTERSECT",VERTEX,{"derivedFrom":[subQ0,subQ5]});Q49=makeQuery(id+"F0.imprint","IMPRINT",FACE,{"disambiguationData":[TD([[makeQuery(id+"F0.imprint","IMPRINT",EDGE,{"disambiguationData":[TD([[subQ6,-1.0]])],"derivedFrom":subQ5}),1.0]])]});}
            var Q50;
            {var subQ5=sQuery(id+"F0.wireOp",EDGE,"E9.top");Q50=makeQuery(id+"F0.imprint","IMPRINT",FACE,{"disambiguationData":[TD([[makeQuery(id+"F0.imprint","IMPRINT",EDGE,{"derivedFrom":subQ5}),1.0]])]});}
            var Q51;
            {var subQ5=sQuery(id+"F0.wireOp",EDGE,"E10.top");Q51=makeQuery(id+"F0.imprint","IMPRINT",FACE,{"disambiguationData":[TD([[makeQuery(id+"F0.imprint","IMPRINT",EDGE,{"derivedFrom":subQ5}),1.0]])]});}
            var Q52;
            {var subQ5=sQuery(id+"F0.wireOp",EDGE,"E18.top");Q52=makeQuery(id+"F0.imprint","IMPRINT",FACE,{"disambiguationData":[TD([[makeQuery(id+"F0.imprint","IMPRINT",EDGE,{"derivedFrom":subQ5}),1.0]])]});}
            var Q53;
            {var subQ5=sQuery(id+"F0.wireOp",EDGE,"E19.top");Q53=makeQuery(id+"F0.imprint","IMPRINT",FACE,{"disambiguationData":[TD([[makeQuery(id+"F0.imprint","IMPRINT",EDGE,{"derivedFrom":subQ5}),1.0]])]});}
            var Q54;
            {var subQ5=sQuery(id+"F0.wireOp",EDGE,"E20.top");Q54=makeQuery(id+"F0.imprint","IMPRINT",FACE,{"disambiguationData":[TD([[makeQuery(id+"F0.imprint","IMPRINT",EDGE,{"derivedFrom":subQ5}),1.0]])]});}
            var Q55;
            {var subQ0=sQuery(id+"F0.wireOp",EDGE,"E5.top");var subQ1=sQuery(id+"F0.wireOp",EDGE,"E2");var subQ2=makeQuery(id+"F0.imprint","INTERSECT",VERTEX,{"derivedFrom":[subQ1,subQ0]});Q55=makeQuery(id+"F0.imprint","IMPRINT",FACE,{"disambiguationData":[TD([[makeQuery(id+"F0.imprint","IMPRINT",EDGE,{"disambiguationData":[TD([[subQ2,1.0]])],"derivedFrom":subQ1}),1.0]])]});}
            var Q56;
            {var subQ0=sQuery(id+"F0.wireOp",EDGE,"E5.top");var subQ1=sQuery(id+"F0.wireOp",EDGE,"E2");var subQ2=makeQuery(id+"F0.imprint","INTERSECT",VERTEX,{"derivedFrom":[subQ1,subQ0]});Q56=makeQuery(id+"F0.imprint","IMPRINT",FACE,{"disambiguationData":[TD([[makeQuery(id+"F0.imprint","IMPRINT",EDGE,{"disambiguationData":[TD([[subQ2,1.0]])],"derivedFrom":subQ1}),-1.0]])]});}
            var Q57;
            {var subQ0=sQuery(id+"F0.wireOp",EDGE,"E20.left");var subQ5=sQuery(id+"F0.wireOp",EDGE,"E7.top");var subQ6=makeQuery(id+"F0.imprint","INTERSECT",VERTEX,{"derivedFrom":[subQ5,subQ0]});Q57=makeQuery(id+"F0.imprint","IMPRINT",FACE,{"disambiguationData":[TD([[makeQuery(id+"F0.imprint","IMPRINT",EDGE,{"disambiguationData":[TD([[subQ6,-1.0]])],"derivedFrom":subQ5}),1.0]])]});}
            var Q58;
            {var subQ5=sQuery(id+"F0.wireOp",EDGE,"E21.top");Q58=makeQuery(id+"F0.imprint","IMPRINT",FACE,{"disambiguationData":[TD([[makeQuery(id+"F0.imprint","IMPRINT",EDGE,{"derivedFrom":subQ5}),1.0]])]});}
            var Q59;
            {var subQ0=sQuery(id+"F0.wireOp",EDGE,"E21.right");var subQ1=sQuery(id+"F0.wireOp",EDGE,"E7.top");var subQ2=makeQuery(id+"F0.imprint","INTERSECT",VERTEX,{"derivedFrom":[subQ1,subQ0]});Q59=makeQuery(id+"F0.imprint","IMPRINT",FACE,{"disambiguationData":[TD([[makeQuery(id+"F0.imprint","IMPRINT",EDGE,{"disambiguationData":[TD([[subQ2,-1.0]])],"derivedFrom":subQ1}),-1.0]])]});}
            var Q60;
            {var subQ0=sQuery(id+"F0.wireOp",EDGE,"E20.right");var subQ1=sQuery(id+"F0.wireOp",EDGE,"E7.top");var subQ2=makeQuery(id+"F0.imprint","INTERSECT",VERTEX,{"derivedFrom":[subQ1,subQ0]});Q60=makeQuery(id+"F0.imprint","IMPRINT",FACE,{"disambiguationData":[TD([[makeQuery(id+"F0.imprint","IMPRINT",EDGE,{"disambiguationData":[TD([[subQ2,-1.0]])],"derivedFrom":subQ1}),-1.0]])]});}
            var Q61;
            {var subQ0=sQuery(id+"F0.wireOp",EDGE,"E19.right");var subQ1=sQuery(id+"F0.wireOp",EDGE,"E7.top");var subQ2=makeQuery(id+"F0.imprint","INTERSECT",VERTEX,{"derivedFrom":[subQ1,subQ0]});Q61=makeQuery(id+"F0.imprint","IMPRINT",FACE,{"disambiguationData":[TD([[makeQuery(id+"F0.imprint","IMPRINT",EDGE,{"disambiguationData":[TD([[subQ2,-1.0]])],"derivedFrom":subQ1}),-1.0]])]});}
            var Q62;
            {var subQ0=sQuery(id+"F0.wireOp",EDGE,"E18.right");var subQ1=sQuery(id+"F0.wireOp",EDGE,"E7.top");var subQ2=makeQuery(id+"F0.imprint","INTERSECT",VERTEX,{"derivedFrom":[subQ1,subQ0]});Q62=makeQuery(id+"F0.imprint","IMPRINT",FACE,{"disambiguationData":[TD([[makeQuery(id+"F0.imprint","IMPRINT",EDGE,{"disambiguationData":[TD([[subQ2,-1.0]])],"derivedFrom":subQ1}),-1.0]])]});}
            var Q63;
            {var subQ0=sQuery(id+"F0.wireOp",EDGE,"E10.right");var subQ1=sQuery(id+"F0.wireOp",EDGE,"E7.top");var subQ2=makeQuery(id+"F0.imprint","INTERSECT",VERTEX,{"derivedFrom":[subQ1,subQ0]});Q63=makeQuery(id+"F0.imprint","IMPRINT",FACE,{"disambiguationData":[TD([[makeQuery(id+"F0.imprint","IMPRINT",EDGE,{"disambiguationData":[TD([[subQ2,-1.0]])],"derivedFrom":subQ1}),-1.0]])]});}
            var Q64;
            {var subQ0=sQuery(id+"F0.wireOp",EDGE,"E9.right");var subQ1=sQuery(id+"F0.wireOp",EDGE,"E7.top");var subQ2=makeQuery(id+"F0.imprint","INTERSECT",VERTEX,{"derivedFrom":[subQ1,subQ0]});Q64=makeQuery(id+"F0.imprint","IMPRINT",FACE,{"disambiguationData":[TD([[makeQuery(id+"F0.imprint","IMPRINT",EDGE,{"disambiguationData":[TD([[subQ2,-1.0]])],"derivedFrom":subQ1}),-1.0]])]});}
            var Q65;
            {var subQ0=sQuery(id+"F0.wireOp",EDGE,"E8.top");var subQ1=sQuery(id+"F0.wireOp",EDGE,"E2");var subQ2=makeQuery(id+"F0.imprint","INTERSECT",VERTEX,{"derivedFrom":[subQ1,subQ0]});Q65=makeQuery(id+"F0.imprint","IMPRINT",FACE,{"disambiguationData":[TD([[makeQuery(id+"F0.imprint","IMPRINT",EDGE,{"disambiguationData":[TD([[subQ2,-1.0]])],"derivedFrom":subQ1}),-1.0]])]});}
            var Q66;
            {var subQ5=sQuery(id+"F0.wireOp",EDGE,"E5.right");Q66=makeQuery(id+"F0.imprint","IMPRINT",FACE,{"disambiguationData":[TD([[makeQuery(id+"F0.imprint","IMPRINT",EDGE,{"derivedFrom":subQ5}),-1.0]])]});}
            var Q67;
            {var subQ0=sQuery(id+"F0.wireOp",EDGE,"E19.left");var subQ5=sQuery(id+"F0.wireOp",EDGE,"E8.top");var subQ6=makeQuery(id+"F0.imprint","INTERSECT",VERTEX,{"derivedFrom":[subQ5,subQ0]});Q67=makeQuery(id+"F0.imprint","IMPRINT",FACE,{"disambiguationData":[TD([[makeQuery(id+"F0.imprint","IMPRINT",EDGE,{"disambiguationData":[TD([[subQ6,-1.0]])],"derivedFrom":subQ5}),-1.0]])]});}
            var Q68;
            {var subQ0=sQuery(id+"F0.wireOp",EDGE,"E5.left");var subQ5=sQuery(id+"F0.wireOp",EDGE,"E8.top");var subQ6=makeQuery(id+"F0.imprint","INTERSECT",VERTEX,{"derivedFrom":[subQ0,subQ5]});Q68=makeQuery(id+"F0.imprint","IMPRINT",FACE,{"disambiguationData":[TD([[makeQuery(id+"F0.imprint","IMPRINT",EDGE,{"disambiguationData":[TD([[subQ6,-1.0]])],"derivedFrom":subQ5}),-1.0]])]});}
            var Q69;
            {var subQ0=sQuery(id+"F0.wireOp",EDGE,"E18.left");var subQ5=sQuery(id+"F0.wireOp",EDGE,"E8.top");var subQ6=makeQuery(id+"F0.imprint","INTERSECT",VERTEX,{"derivedFrom":[subQ5,subQ0]});Q69=makeQuery(id+"F0.imprint","IMPRINT",FACE,{"disambiguationData":[TD([[makeQuery(id+"F0.imprint","IMPRINT",EDGE,{"disambiguationData":[TD([[subQ6,-1.0]])],"derivedFrom":subQ5}),-1.0]])]});}
            var Q70;
            {var subQ0=sQuery(id+"F0.wireOp",EDGE,"E20.left");var subQ5=sQuery(id+"F0.wireOp",EDGE,"E8.top");var subQ6=makeQuery(id+"F0.imprint","INTERSECT",VERTEX,{"derivedFrom":[subQ5,subQ0]});Q70=makeQuery(id+"F0.imprint","IMPRINT",FACE,{"disambiguationData":[TD([[makeQuery(id+"F0.imprint","IMPRINT",EDGE,{"disambiguationData":[TD([[subQ6,-1.0]])],"derivedFrom":subQ5}),-1.0]])]});}
            var Q71;
            {var subQ0=sQuery(id+"F0.wireOp",EDGE,"E10.left");var subQ5=sQuery(id+"F0.wireOp",EDGE,"E8.top");var subQ6=makeQuery(id+"F0.imprint","INTERSECT",VERTEX,{"derivedFrom":[subQ5,subQ0]});Q71=makeQuery(id+"F0.imprint","IMPRINT",FACE,{"disambiguationData":[TD([[makeQuery(id+"F0.imprint","IMPRINT",EDGE,{"disambiguationData":[TD([[subQ6,-1.0]])],"derivedFrom":subQ5}),-1.0]])]});}
            var Q72;
            {var subQ0=sQuery(id+"F0.wireOp",EDGE,"E9.left");var subQ5=sQuery(id+"F0.wireOp",EDGE,"E8.top");var subQ6=makeQuery(id+"F0.imprint","INTERSECT",VERTEX,{"derivedFrom":[subQ5,subQ0]});Q72=makeQuery(id+"F0.imprint","IMPRINT",FACE,{"disambiguationData":[TD([[makeQuery(id+"F0.imprint","IMPRINT",EDGE,{"disambiguationData":[TD([[subQ6,-1.0]])],"derivedFrom":subQ5}),-1.0]])]});}
            var Q73;
            {var subQ5=sQuery(id+"F0.wireOp",EDGE,"E20.bottom");Q73=makeQuery(id+"F0.imprint","IMPRINT",FACE,{"disambiguationData":[TD([[makeQuery(id+"F0.imprint","IMPRINT",EDGE,{"derivedFrom":subQ5}),-1.0]])]});}
            var Q74;
            {var subQ5=sQuery(id+"F0.wireOp",EDGE,"E10.bottom");Q74=makeQuery(id+"F0.imprint","IMPRINT",FACE,{"disambiguationData":[TD([[makeQuery(id+"F0.imprint","IMPRINT",EDGE,{"derivedFrom":subQ5}),-1.0]])]});}
            var Q75;
            {var subQ5=sQuery(id+"F0.wireOp",EDGE,"E19.bottom");Q75=makeQuery(id+"F0.imprint","IMPRINT",FACE,{"disambiguationData":[TD([[makeQuery(id+"F0.imprint","IMPRINT",EDGE,{"derivedFrom":subQ5}),-1.0]])]});}
            var Q76;
            {var subQ5=sQuery(id+"F0.wireOp",EDGE,"E9.bottom");Q76=makeQuery(id+"F0.imprint","IMPRINT",FACE,{"disambiguationData":[TD([[makeQuery(id+"F0.imprint","IMPRINT",EDGE,{"derivedFrom":subQ5}),-1.0]])]});}
            var Q77;
            {var subQ5=sQuery(id+"F0.wireOp",EDGE,"E21.bottom");Q77=makeQuery(id+"F0.imprint","IMPRINT",FACE,{"disambiguationData":[TD([[makeQuery(id+"F0.imprint","IMPRINT",EDGE,{"derivedFrom":subQ5}),-1.0]])]});}
            var Q78;
            {var subQ5=sQuery(id+"F0.wireOp",EDGE,"E18.bottom");Q78=makeQuery(id+"F0.imprint","IMPRINT",FACE,{"disambiguationData":[TD([[makeQuery(id+"F0.imprint","IMPRINT",EDGE,{"derivedFrom":subQ5}),-1.0]])]});}
            var Q79;
            {var subQ0=sQuery(id+"F0.wireOp",EDGE,"E5.bottom");var subQ1=sQuery(id+"F0.wireOp",EDGE,"E2");var subQ2=makeQuery(id+"F0.imprint","INTERSECT",VERTEX,{"derivedFrom":[subQ1,subQ0]});Q79=makeQuery(id+"F0.imprint","IMPRINT",FACE,{"disambiguationData":[TD([[makeQuery(id+"F0.imprint","IMPRINT",EDGE,{"disambiguationData":[TD([[subQ2,-1.0]])],"derivedFrom":subQ1}),1.0]])]});}
            var Q80;
            {var subQ0=sQuery(id+"F0.wireOp",EDGE,"E5.bottom");var subQ1=sQuery(id+"F0.wireOp",EDGE,"E2");var subQ2=makeQuery(id+"F0.imprint","INTERSECT",VERTEX,{"derivedFrom":[subQ1,subQ0]});Q80=makeQuery(id+"F0.imprint","IMPRINT",FACE,{"disambiguationData":[TD([[makeQuery(id+"F0.imprint","IMPRINT",EDGE,{"disambiguationData":[TD([[subQ2,-1.0]])],"derivedFrom":subQ1}),-1.0]])]});}
            var Q81;
            {var subQ5=sQuery(id+"F0.wireOp",EDGE,"E26.left");Q81=makeQuery(id+"F0.imprint","IMPRINT",FACE,{"disambiguationData":[TD([[makeQuery(id+"F0.imprint","IMPRINT",EDGE,{"derivedFrom":subQ5}),1.0]])]});}
            var Q82;
            {var subQ5=sQuery(id+"F0.wireOp",EDGE,"E27.top");Q82=makeQuery(id+"F0.imprint","IMPRINT",FACE,{"disambiguationData":[TD([[makeQuery(id+"F0.imprint","IMPRINT",EDGE,{"derivedFrom":subQ5}),1.0]])]});}
            extrude(context, id + "F1", {"entities" : qUnion([Q0, Q1, Q2, Q3, Q4, Q5, Q6, Q7, Q8, Q9, Q10, Q11, Q12, Q13, Q14, Q15, Q16, Q17, Q18, Q19, Q20, Q21, Q22, Q23, Q24, Q25, Q26, Q27, Q28, Q29, Q30, Q31, Q32, Q33, Q34, Q35, Q36, Q37, Q38, Q39, Q40, Q41, Q42, Q43, Q44, Q45, Q46, Q47, Q48, Q49, Q50, Q51, Q52, Q53, Q54, Q55, Q56, Q57, Q58, Q59, Q60, Q61, Q62, Q63, Q64, Q65, Q66, Q67, Q68, Q69, Q70, Q71, Q72, Q73, Q74, Q75, Q76, Q77, Q78, Q79, Q80, Q81, Q82]), "depth" : 2.5 * mm});
        }
        {
            var Q0;
            Q0=makeQuery(id+"F1.opExtrude","CAP_EDGE",EDGE,{"disambiguationData":[OSD([sQuery(id+"F0.wireOp",EDGE,"E9.right")])],"isStart":false});
            var Q1;
            Q1=makeQuery(id+"F1.opExtrude","CAP_EDGE",EDGE,{"disambiguationData":[OSD([sQuery(id+"F0.wireOp",EDGE,"E9.left")])],"isStart":false});
            var Q2;
            Q2=makeQuery(id+"F1.opExtrude","CAP_EDGE",EDGE,{"disambiguationData":[OSD([sQuery(id+"F0.wireOp",EDGE,"E10.right")])],"isStart":false});
            var Q3;
            Q3=makeQuery(id+"F1.opExtrude","CAP_EDGE",EDGE,{"disambiguationData":[OSD([sQuery(id+"F0.wireOp",EDGE,"E10.left")])],"isStart":false});
            var Q4;
            Q4=makeQuery(id+"F1.opExtrude","CAP_EDGE",EDGE,{"disambiguationData":[OSD([sQuery(id+"F0.wireOp",EDGE,"E18.right")])],"isStart":false});
            var Q5;
            Q5=makeQuery(id+"F1.opExtrude","CAP_EDGE",EDGE,{"disambiguationData":[OSD([sQuery(id+"F0.wireOp",EDGE,"E19.right")])],"isStart":false});
            var Q6;
            Q6=makeQuery(id+"F1.opExtrude","CAP_EDGE",EDGE,{"disambiguationData":[OSD([sQuery(id+"F0.wireOp",EDGE,"E19.left")])],"isStart":false});
            var Q7;
            Q7=makeQuery(id+"F1.opExtrude","CAP_EDGE",EDGE,{"disambiguationData":[OSD([sQuery(id+"F0.wireOp",EDGE,"E20.right")])],"isStart":false});
            var Q8;
            Q8=makeQuery(id+"F1.opExtrude","CAP_EDGE",EDGE,{"disambiguationData":[OSD([sQuery(id+"F0.wireOp",EDGE,"E21.right")])],"isStart":false});
            var Q9;
            Q9=makeQuery(id+"F1.opExtrude","CAP_EDGE",EDGE,{"disambiguationData":[OSD([sQuery(id+"F0.wireOp",EDGE,"E21.left")])],"isStart":false});
            var Q10;
            Q10=makeQuery(id+"F1.opExtrude","CAP_EDGE",EDGE,{"disambiguationData":[OSD([sQuery(id+"F0.wireOp",EDGE,"E22.left")])],"isStart":false});
            var Q11;
            Q11=makeQuery(id+"F1.opExtrude","CAP_EDGE",EDGE,{"disambiguationData":[OSD([sQuery(id+"F0.wireOp",EDGE,"E22.right")])],"isStart":false});
            var Q12;
            Q12=makeQuery(id+"F1.opExtrude","CAP_EDGE",EDGE,{"disambiguationData":[OSD([sQuery(id+"F0.wireOp",EDGE,"E23.left")])],"isStart":false});
            var Q13;
            Q13=makeQuery(id+"F1.opExtrude","CAP_EDGE",EDGE,{"disambiguationData":[OSD([sQuery(id+"F0.wireOp",EDGE,"E23.right")])],"isStart":false});
            var Q14;
            Q14=makeQuery(id+"F1.opExtrude","CAP_EDGE",EDGE,{"disambiguationData":[OSD([sQuery(id+"F0.wireOp",EDGE,"E24.left")])],"isStart":false});
            var Q15;
            Q15=makeQuery(id+"F1.opExtrude","CAP_EDGE",EDGE,{"disambiguationData":[OSD([sQuery(id+"F0.wireOp",EDGE,"E24.right")])],"isStart":false});
            var Q16;
            Q16=makeQuery(id+"F1.opExtrude","CAP_EDGE",EDGE,{"disambiguationData":[OSD([sQuery(id+"F0.wireOp",EDGE,"E25.left")])],"isStart":false});
            var Q17;
            {var subQ0=sQuery(id+"F0.wireOp",EDGE,"E25.right");Q17=makeQuery(id+"F1.opExtrude","CAP_EDGE",EDGE,{"disambiguationData":[OSD([subQ0]),TDD([makeQuery(id+"F0.imprint","IMPRINT",EDGE,{"disambiguationData":[TD([[makeQuery(id+"F0.imprint","INTERSECT",VERTEX,{"derivedFrom":[sQuery(id+"F0.wireOp",EDGE,"E8.top"),subQ0]}),-1.0]])],"derivedFrom":subQ0})])],"isStart":false});}
            var Q18;
            {var subQ0=sQuery(id+"F0.wireOp",EDGE,"E25.right");Q18=makeQuery(id+"F1.opExtrude","CAP_EDGE",EDGE,{"disambiguationData":[OSD([subQ0]),TDD([makeQuery(id+"F0.imprint","IMPRINT",EDGE,{"disambiguationData":[TD([[makeQuery(id+"F0.imprint","INTERSECT",VERTEX,{"derivedFrom":[sQuery(id+"F0.wireOp",EDGE,"E7.top"),subQ0]}),1.0]])],"derivedFrom":subQ0})])],"isStart":false});}
            var Q19;
            Q19=makeQuery(id+"F1.opExtrude","CAP_EDGE",EDGE,{"disambiguationData":[OSD([sQuery(id+"F0.wireOp",EDGE,"E27.left")])],"isStart":false});
            var Q20;
            Q20=makeQuery(id+"F1.opExtrude","CAP_EDGE",EDGE,{"disambiguationData":[OSD([sQuery(id+"F0.wireOp",EDGE,"E27.right")])],"isStart":false});
            var Q21;
            {var subQ0=sQuery(id+"F0.wireOp",EDGE,"E26.bottom");Q21=makeQuery(id+"F1.opExtrude","CAP_EDGE",EDGE,{"disambiguationData":[OSD([subQ0]),TDD([makeQuery(id+"F0.imprint","IMPRINT",EDGE,{"disambiguationData":[TD([[makeQuery(id+"F0.imprint","INTERSECT",VERTEX,{"derivedFrom":[sQuery(id+"F0.wireOp",EDGE,"E25.right"),subQ0]}),-1.0]])],"derivedFrom":subQ0})])],"isStart":false});}
            var Q22;
            {var subQ0=sQuery(id+"F0.wireOp",EDGE,"E26.bottom");Q22=makeQuery(id+"F1.opExtrude","CAP_EDGE",EDGE,{"disambiguationData":[OSD([subQ0]),TDD([makeQuery(id+"F0.imprint","IMPRINT",EDGE,{"disambiguationData":[TD([[makeQuery(id+"F0.imprint","INTERSECT",VERTEX,{"derivedFrom":[subQ0,sQuery(id+"F0.wireOp",EDGE,"E26.right")]}),1.0]])],"derivedFrom":subQ0})])],"isStart":false});}
            var Q23;
            Q23=makeQuery(id+"F1.opExtrude","CAP_EDGE",EDGE,{"disambiguationData":[OSD([sQuery(id+"F0.wireOp",EDGE,"E26.top")])],"isStart":false});
            var Q24;
            Q24=makeQuery(id+"F1.opExtrude","CAP_EDGE",EDGE,{"disambiguationData":[OSD([sQuery(id+"F0.wireOp",EDGE,"E11.right")])],"isStart":false});
            var Q25;
            Q25=makeQuery(id+"F1.opExtrude","CAP_EDGE",EDGE,{"disambiguationData":[OSD([sQuery(id+"F0.wireOp",EDGE,"E5.left")])],"isStart":false});
            var Q26;
            Q26=makeQuery(id+"F1.opExtrude","CAP_EDGE",EDGE,{"disambiguationData":[OSD([sQuery(id+"F0.wireOp",EDGE,"E6.right")])],"isStart":false});
            var Q27;
            Q27=makeQuery(id+"F1.opExtrude","CAP_EDGE",EDGE,{"disambiguationData":[OSD([sQuery(id+"F0.wireOp",EDGE,"E6.left"),sQuery(id+"F0.wireOp",EDGE,"E7.right"),sQuery(id+"F0.wireOp",EDGE,"E8.right")])],"isStart":false});
            var Q28;
            Q28=makeQuery(id+"F1.opExtrude","CAP_EDGE",EDGE,{"disambiguationData":[OSD([sQuery(id+"F0.wireOp",EDGE,"E6.left"),sQuery(id+"F0.wireOp",EDGE,"E7.right"),sQuery(id+"F0.wireOp",EDGE,"E8.right")])],"isStart":true});
            var Q29;
            Q29=makeQuery(id+"F1.opExtrude","CAP_EDGE",EDGE,{"disambiguationData":[OSD([sQuery(id+"F0.wireOp",EDGE,"E6.right")])],"isStart":true});
            var Q30;
            Q30=makeQuery(id+"F1.opExtrude","CAP_EDGE",EDGE,{"disambiguationData":[OSD([sQuery(id+"F0.wireOp",EDGE,"E22.left")])],"isStart":true});
            var Q31;
            Q31=makeQuery(id+"F1.opExtrude","CAP_EDGE",EDGE,{"disambiguationData":[OSD([sQuery(id+"F0.wireOp",EDGE,"E22.right")])],"isStart":true});
            var Q32;
            Q32=makeQuery(id+"F1.opExtrude","CAP_EDGE",EDGE,{"disambiguationData":[OSD([sQuery(id+"F0.wireOp",EDGE,"E23.left")])],"isStart":true});
            var Q33;
            Q33=makeQuery(id+"F1.opExtrude","CAP_EDGE",EDGE,{"disambiguationData":[OSD([sQuery(id+"F0.wireOp",EDGE,"E23.right")])],"isStart":true});
            var Q34;
            Q34=makeQuery(id+"F1.opExtrude","CAP_EDGE",EDGE,{"disambiguationData":[OSD([sQuery(id+"F0.wireOp",EDGE,"E24.left")])],"isStart":true});
            var Q35;
            Q35=makeQuery(id+"F1.opExtrude","CAP_EDGE",EDGE,{"disambiguationData":[OSD([sQuery(id+"F0.wireOp",EDGE,"E24.right")])],"isStart":true});
            var Q36;
            {var subQ0=sQuery(id+"F0.wireOp",EDGE,"E25.right");Q36=makeQuery(id+"F1.opExtrude","CAP_EDGE",EDGE,{"disambiguationData":[OSD([subQ0]),TDD([makeQuery(id+"F0.imprint","IMPRINT",EDGE,{"disambiguationData":[TD([[makeQuery(id+"F0.imprint","INTERSECT",VERTEX,{"derivedFrom":[sQuery(id+"F0.wireOp",EDGE,"E7.top"),subQ0]}),1.0]])],"derivedFrom":subQ0})])],"isStart":true});}
            var Q37;
            {var subQ0=sQuery(id+"F0.wireOp",EDGE,"E25.right");Q37=makeQuery(id+"F1.opExtrude","CAP_EDGE",EDGE,{"disambiguationData":[OSD([subQ0]),TDD([makeQuery(id+"F0.imprint","IMPRINT",EDGE,{"disambiguationData":[TD([[makeQuery(id+"F0.imprint","INTERSECT",VERTEX,{"derivedFrom":[sQuery(id+"F0.wireOp",EDGE,"E8.top"),subQ0]}),-1.0]])],"derivedFrom":subQ0})])],"isStart":true});}
            var Q38;
            {var subQ0=sQuery(id+"F0.wireOp",EDGE,"E26.bottom");Q38=makeQuery(id+"F1.opExtrude","CAP_EDGE",EDGE,{"disambiguationData":[OSD([subQ0]),TDD([makeQuery(id+"F0.imprint","IMPRINT",EDGE,{"disambiguationData":[TD([[makeQuery(id+"F0.imprint","INTERSECT",VERTEX,{"derivedFrom":[sQuery(id+"F0.wireOp",EDGE,"E25.right"),subQ0]}),-1.0]])],"derivedFrom":subQ0})])],"isStart":true});}
            var Q39;
            Q39=makeQuery(id+"F1.opExtrude","CAP_EDGE",EDGE,{"disambiguationData":[OSD([sQuery(id+"F0.wireOp",EDGE,"E27.left")])],"isStart":true});
            var Q40;
            {var subQ0=sQuery(id+"F0.wireOp",EDGE,"E26.bottom");Q40=makeQuery(id+"F1.opExtrude","CAP_EDGE",EDGE,{"disambiguationData":[OSD([subQ0]),TDD([makeQuery(id+"F0.imprint","IMPRINT",EDGE,{"disambiguationData":[TD([[makeQuery(id+"F0.imprint","INTERSECT",VERTEX,{"derivedFrom":[subQ0,sQuery(id+"F0.wireOp",EDGE,"E26.right")]}),1.0]])],"derivedFrom":subQ0})])],"isStart":true});}
            var Q41;
            Q41=makeQuery(id+"F1.opExtrude","CAP_EDGE",EDGE,{"disambiguationData":[OSD([sQuery(id+"F0.wireOp",EDGE,"E26.top")])],"isStart":true});
            var Q42;
            Q42=makeQuery(id+"F1.opExtrude","CAP_EDGE",EDGE,{"disambiguationData":[OSD([sQuery(id+"F0.wireOp",EDGE,"E25.left")])],"isStart":true});
            var Q43;
            Q43=makeQuery(id+"F1.opExtrude","CAP_EDGE",EDGE,{"disambiguationData":[OSD([sQuery(id+"F0.wireOp",EDGE,"E27.right")])],"isStart":true});
            var Q44;
            Q44=makeQuery(id+"F1.opExtrude","CAP_EDGE",EDGE,{"disambiguationData":[OSD([sQuery(id+"F0.wireOp",EDGE,"E11.right")])],"isStart":true});
            var Q45;
            Q45=makeQuery(id+"F1.opExtrude","CAP_EDGE",EDGE,{"disambiguationData":[OSD([sQuery(id+"F0.wireOp",EDGE,"E11.left")])],"isStart":true});
            var Q46;
            Q46=makeQuery(id+"F1.opExtrude","CAP_EDGE",EDGE,{"disambiguationData":[OSD([sQuery(id+"F0.wireOp",EDGE,"E21.left")])],"isStart":true});
            var Q47;
            Q47=makeQuery(id+"F1.opExtrude","CAP_EDGE",EDGE,{"disambiguationData":[OSD([sQuery(id+"F0.wireOp",EDGE,"E21.right")])],"isStart":true});
            var Q48;
            Q48=makeQuery(id+"F1.opExtrude","CAP_EDGE",EDGE,{"disambiguationData":[OSD([sQuery(id+"F0.wireOp",EDGE,"E20.right")])],"isStart":true});
            var Q49;
            Q49=makeQuery(id+"F1.opExtrude","CAP_EDGE",EDGE,{"disambiguationData":[OSD([sQuery(id+"F0.wireOp",EDGE,"E20.left")])],"isStart":true});
            var Q50;
            Q50=makeQuery(id+"F1.opExtrude","CAP_EDGE",EDGE,{"disambiguationData":[OSD([sQuery(id+"F0.wireOp",EDGE,"E19.left")])],"isStart":true});
            var Q51;
            Q51=makeQuery(id+"F1.opExtrude","CAP_EDGE",EDGE,{"disambiguationData":[OSD([sQuery(id+"F0.wireOp",EDGE,"E19.right")])],"isStart":true});
            var Q52;
            Q52=makeQuery(id+"F1.opExtrude","CAP_EDGE",EDGE,{"disambiguationData":[OSD([sQuery(id+"F0.wireOp",EDGE,"E18.right")])],"isStart":true});
            var Q53;
            Q53=makeQuery(id+"F1.opExtrude","CAP_EDGE",EDGE,{"disambiguationData":[OSD([sQuery(id+"F0.wireOp",EDGE,"E10.left")])],"isStart":true});
            var Q54;
            Q54=makeQuery(id+"F1.opExtrude","CAP_EDGE",EDGE,{"disambiguationData":[OSD([sQuery(id+"F0.wireOp",EDGE,"E10.right")])],"isStart":true});
            var Q55;
            Q55=makeQuery(id+"F1.opExtrude","CAP_EDGE",EDGE,{"disambiguationData":[OSD([sQuery(id+"F0.wireOp",EDGE,"E18.left")])],"isStart":true});
            var Q56;
            Q56=makeQuery(id+"F1.opExtrude","CAP_EDGE",EDGE,{"disambiguationData":[OSD([sQuery(id+"F0.wireOp",EDGE,"E9.left")])],"isStart":true});
            var Q57;
            Q57=makeQuery(id+"F1.opExtrude","CAP_EDGE",EDGE,{"disambiguationData":[OSD([sQuery(id+"F0.wireOp",EDGE,"E9.right")])],"isStart":true});
            var Q58;
            Q58=makeQuery(id+"F1.opExtrude","CAP_EDGE",EDGE,{"disambiguationData":[OSD([sQuery(id+"F0.wireOp",EDGE,"E5.left")])],"isStart":true});
            var Q59;
            Q59=makeQuery(id+"F1.opExtrude","CAP_EDGE",EDGE,{"disambiguationData":[OSD([sQuery(id+"F0.wireOp",EDGE,"E5.right"),sQuery(id+"F0.wireOp",EDGE,"E7.left"),sQuery(id+"F0.wireOp",EDGE,"E8.left")])],"isStart":false});
            var Q60;
            Q60=makeQuery(id+"F1.opExtrude","CAP_EDGE",EDGE,{"disambiguationData":[OSD([sQuery(id+"F0.wireOp",EDGE,"E5.right"),sQuery(id+"F0.wireOp",EDGE,"E7.left"),sQuery(id+"F0.wireOp",EDGE,"E8.left")])],"isStart":true});
            var Q61;
            Q61=makeQuery(id+"F1.opExtrude","CAP_EDGE",EDGE,{"disambiguationData":[OSD([sQuery(id+"F0.wireOp",EDGE,"E18.left")])],"isStart":false});
            var Q62;
            Q62=makeQuery(id+"F1.opExtrude","CAP_EDGE",EDGE,{"disambiguationData":[OSD([sQuery(id+"F0.wireOp",EDGE,"E20.left")])],"isStart":false});
            var Q63;
            Q63=makeQuery(id+"F1.opExtrude","CAP_EDGE",EDGE,{"disambiguationData":[OSD([sQuery(id+"F0.wireOp",EDGE,"E15")])],"isStart":false});
            var Q64;
            Q64=makeQuery(id+"F1.opExtrude","CAP_EDGE",EDGE,{"disambiguationData":[OSD([sQuery(id+"F0.wireOp",EDGE,"E16")])],"isStart":false});
            var Q65;
            Q65=makeQuery(id+"F1.opExtrude","CAP_EDGE",EDGE,{"disambiguationData":[OSD([sQuery(id+"F0.wireOp",EDGE,"E16")])],"isStart":true});
            var Q66;
            Q66=makeQuery(id+"F1.opExtrude","CAP_EDGE",EDGE,{"disambiguationData":[OSD([sQuery(id+"F0.wireOp",EDGE,"E15")])],"isStart":true});
            fillet(context, id + "F2", {"entities" : qUnion([Q0, Q1, Q2, Q3, Q4, Q5, Q6, Q7, Q8, Q9, Q10, Q11, Q12, Q13, Q14, Q15, Q16, Q17, Q18, Q19, Q20, Q21, Q22, Q23, Q24, Q25, Q26, Q27, Q28, Q29, Q30, Q31, Q32, Q33, Q34, Q35, Q36, Q37, Q38, Q39, Q40, Q41, Q42, Q43, Q44, Q45, Q46, Q47, Q48, Q49, Q50, Q51, Q52, Q53, Q54, Q55, Q56, Q57, Q58, Q59, Q60, Q61, Q62, Q63, Q64, Q65, Q66]), "radius" : 1.25 * mm, "tangentPropagation" : true, "allowEdgeOverflow" : false});
        }
        {
            var Q0;
            Q0=makeQuery(id+"F1.opExtrude","CAP_EDGE",EDGE,{"disambiguationData":[OSD([sQuery(id+"F0.wireOp",EDGE,"E13")])],"isStart":false});
            fillet(context, id + "F3", {"entities" : qUnion([Q0]), "radius" : 1 * mm, "tangentPropagation" : true, "allowEdgeOverflow" : false});
        }
    });
